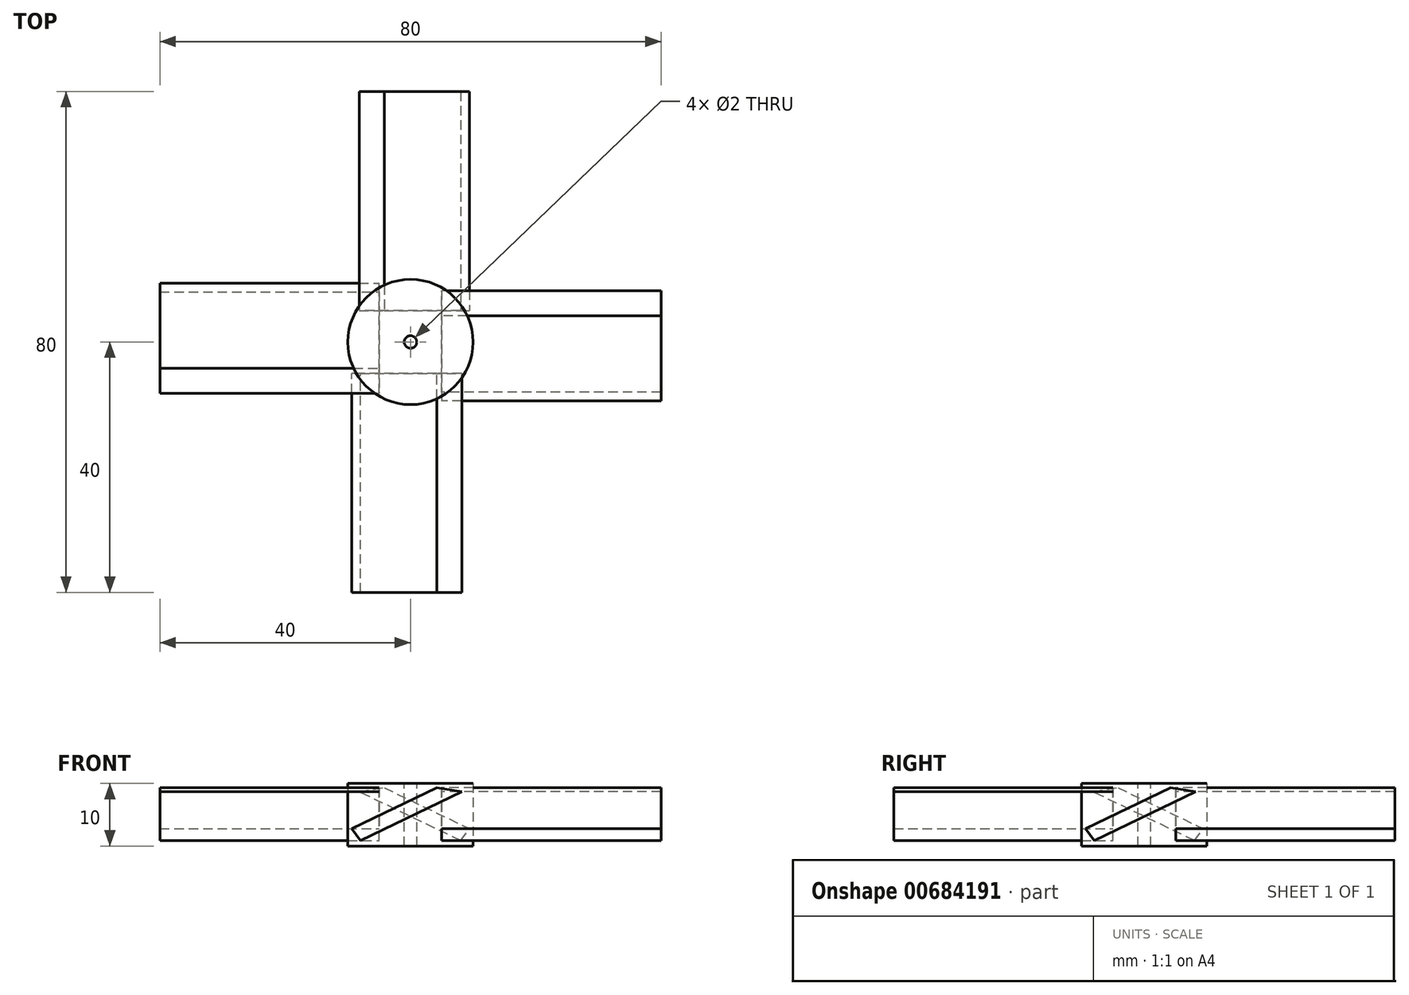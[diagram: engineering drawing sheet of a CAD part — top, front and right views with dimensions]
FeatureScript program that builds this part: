
annotation { "Feature Type Name" : "Feature", "Feature Type Description" : "" }
export const myFeature = defineFeature(function(context is Context, id is Id, definition is map)
    precondition{}
    {
        {
            var Q0;
            Q0=qCreatedBy(makeId("Top.planeOp"),FACE);
            var sketch = newSketch(context, id + "F0", { "sketchPlane" : qUnion([Q0])});
            skCircle(sketch, "E0", {"center": v(0, 0) * mm, "radius": 10 * mm});
            skSolve(sketch);
        }
        {
            var Q0;
            Q0=makeQuery(id+"F0.imprint","IMPRINT",FACE,{"disambiguationData":[TD([[makeQuery(id+"F0.imprint","IMPRINT",EDGE,{"derivedFrom":sQuery(id+"F0.wireOp",EDGE,"E0")}),1.0]])]});
            extrude(context, id + "F1", {"entities" : qUnion([Q0]), "depth" : 10 * mm, "offsetDistance" : 25 * mm});
        }
        {
            var Q0;
            Q0=makeQuery(id+"F1.opExtrude","CAP_FACE",FACE,{"disambiguationData":[OSD([sQuery(id+"F0.wireOp",EDGE,"E0")])],"isStart":false});
            var sketch = newSketch(context, id + "F2", { "sketchPlane" : qUnion([Q0])});
            skCircle(sketch, "E1", {"center": v(0, 0) * mm, "radius": 1 * mm});
            skSolve(sketch);
        }
        {
            var Q0;
            Q0 = qSketchRegion(id + "F2", true);
            extrude(context, id + "F3", {"entities" : qUnion([Q0]), "operationType" : NewBodyOperationType.REMOVE, "oppositeDirection" : true, "depth" : 25 * mm, "offsetDistance" : 25 * mm});
        }
        {
            var Q0;
            Q0=qCreatedBy(makeId("Front.planeOp"),FACE);
            var Q1;
            Q1 = qBodyType(qCreatedBy(id + "F5" ,EDGE), BodyType.WIRE);
            cPlane(context, id + "F4", {"entities" : qUnion([Q0, Q1]), "cplaneType" : CPlaneType.OFFSET, "offset" : 5 * mm, "width" : 150 * mm, "height" : 150 * mm});
        }
        {
            var Q0;
            Q0=qCreatedBy(id+"F4.planeOp",FACE);
            var sketch = newSketch(context, id + "F5", { "sketchPlane" : qUnion([Q0])});
            skLineSegment(sketch, "E2", {"start": v(4.2, 9.32) * mm, "end": v(-9.41, 2.76) * mm});
            skLineSegment(sketch, "E3", {"start": v(-8.02, 0.85) * mm, "end": v(-9.41, 2.76) * mm});
            skLineSegment(sketch, "E4", {"start": v(-8.02, 0.85) * mm, "end": v(8.2, 8.66) * mm});
            skLineSegment(sketch, "E5", {"start": v(8.2, 8.66) * mm, "end": v(4.2, 9.32) * mm});
            skSolve(sketch);
        }
        {
            var Q0;
            Q0=qCreatedBy(makeId("Right.planeOp"),FACE);
            var sketch = newSketch(context, id + "F6", { "sketchPlane" : qUnion([Q0])});
            skLineSegment(sketch, "E6", {"start": v(0, 57.65) * mm, "end": v(0, -41.97) * mm});
            skSolve(sketch);
        }
        {
            var Q0;
            Q0 = qSketchRegion(id + "F5", true);
            extrude(context, id + "F7", {"entities" : qUnion([Q0]), "depth" : 35 * mm, "offsetDistance" : 25 * mm});
        }
        {
            var Q0;
            Q0=makeQuery(id+"F1.opExtrude","SWEPT_BODY",BODY,{"disambiguationData":[OSD([sQuery(id+"F0.wireOp",EDGE,"E0")])]});
            var Q1;
            Q1=makeQuery(id+"F7.opExtrude","SWEPT_BODY",BODY,{"disambiguationData":[OSD([sQuery(id+"F5.wireOp",EDGE,"E2"),sQuery(id+"F5.wireOp",EDGE,"E3"),sQuery(id+"F5.wireOp",EDGE,"E4"),sQuery(id+"F5.wireOp",EDGE,"E5")])]});
            var Q2;
            Q2=sQuery(id+"F6.wireOp",EDGE,"E6");
            circularPattern(context, id + "F8", {"entities" : qUnion([Q0, Q1]), "axis" : qUnion([Q2]), "angle" : 360 * degree, "instanceCount" : 4, "oppositeDirection" : true, "equalSpace" : true});
        }
    });
